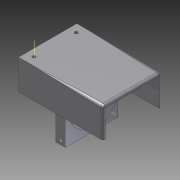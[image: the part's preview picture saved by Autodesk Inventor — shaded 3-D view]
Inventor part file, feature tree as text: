
AUTODESK INVENTOR PART (.ipt)
format: ipt  version: 2012 (Build 160160000, 160)  size: 290,816 bytes
history: native  units: mm
features: extrude x13, sketch x13, reference x9, projected_geometry x9, plane x4, fillet x3, other x2
ambient origin geometry x8: Origin, YZ Plane, XZ Plane, XY Plane, X Axis, Y Axis, Z Axis, Center Point
bodies: Solid1 (feature_tree)
feature tree (53):
  extrude  "Extrusion1"  Depth=2.0mm TaperAngle=0.0deg
  extrude  "Extrusion2"  TaperAngle=45.0deg  [1 undecoded]
  extrude  "Extrusion3"  Depth=9.0mm
  sketch  "Sketch4"  dims[d8=2.0mm d9=0.0mm d10=8.0mm]
  plane  "Work Plane1"
  plane  "Work Plane2"
  extrude  "Extrusion4"  Depth=8.0mm
  extrude  "Extrusion5"  Depth=0.3mm TaperAngle=0.0deg
  extrude  "Extrusion6"  Depth=0.3mm
  extrude  "Extrusion7"  Depth=0.3mm
  extrude  "Extrusion8"  Depth=0.3mm TaperAngle=0.0deg
  extrude  "Extrusion9"  Depth=7.4mm
  extrude  "Extrusion10"  Depth=3.25mm
  plane  "Work Plane3"
  extrude  "Extrusion12"  Depth=5.0mm TaperAngle=0.0deg
  extrude  "Extrusion13"  Depth=0.3mm TaperAngle=0.0deg
  sketch  "Sketch18"  dims[d45=0.3mm d46=0.0mm d47=0.3mm d48=0.0mm d55=2.0mm d56=0.0mm d57=0.0mm d58=2.0mm d59=2.0mm]
  plane  "Work Plane4"
  extrude  "Extrusion14"  Depth=0.3mm TaperAngle=0.0deg
  fillet  "Fillet6"  Radius=2.0mm
  fillet  "Fillet7"  [1 undecoded]
  other  "Work Axis1"
  other  "Work Axis2"
  fillet  "Fillet8"  [1 undecoded]
  sketch  "Sketch1"  dims[d0=24.0mm d1=0.0mm d2=2.0mm d3=0.0mm]
  reference  "Reference1"
  reference  "Reference2"
  sketch  "Sketch2"  dims[d4=45.0deg d5=45.0deg]
  projected_geometry  "Projected Loop1"
  projected_geometry  "Projected Loop2"
  sketch  "Sketch3"  dims[d6=9.0mm d7=9.0mm]
  projected_geometry  "Projected Loop3"
  reference  "Reference3"
  reference  "Reference4"
  sketch  "Sketch6"  dims[d11=2.0mm d12=0.0mm d13=0.3mm d14=0.0mm]
  sketch  "Sketch7"  dims[d16=0.5mm d17=0.0mm d19=0.3mm]
  reference  "Reference8"
  sketch  "Sketch8"  dims[d21=0.3mm d22=0.3mm]
  sketch  "Sketch9"  dims[d23=0.5mm d24=0.0mm d25=0.3mm d26=0.0mm]
  projected_geometry  "Projected Loop4"
  sketch  "Sketch11"  dims[d27=0.3mm d28=7.4mm]
  projected_geometry  "Projected Loop5"
  sketch  "Sketch12"  dims[d29=3.7mm d30=3.25mm]
  sketch  "Sketch15"  dims[d31=2.5mm d32=5.0mm d33=0.0mm]
  projected_geometry  "Projected Loop9"
  sketch  "Sketch16"  dims[d34=5.0mm d35=0.0mm d43=0.3mm d44=0.0mm]
  reference  "Reference9"
  reference  "Reference10"
  projected_geometry  "Projected Loop10"
  projected_geometry  "Projected Loop11"
  projected_geometry  "Projected Loop12"
  reference  "Reference13"
  reference  "Reference14"
note: 3 required parameter values undecoded (feature->parameter linkage not recoverable at this tier; creation-order binding heuristic only, values carry confidence <= 0.55)
